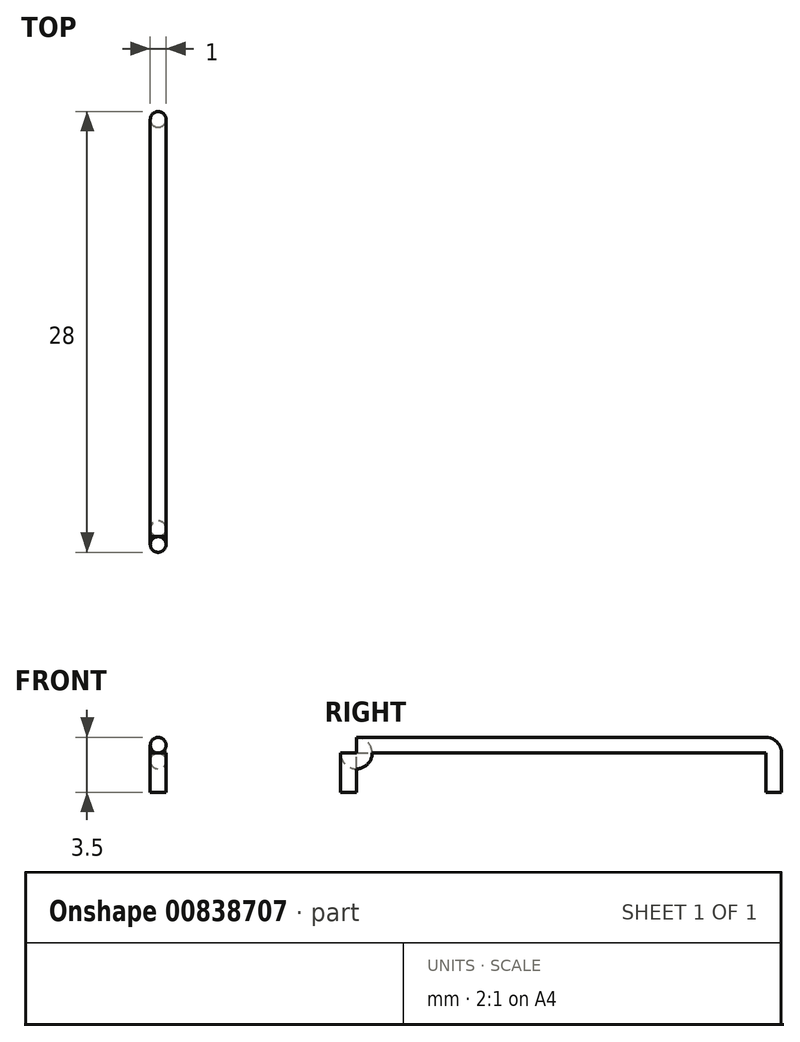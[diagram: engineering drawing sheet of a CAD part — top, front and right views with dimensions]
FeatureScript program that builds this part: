
annotation { "Feature Type Name" : "Feature", "Feature Type Description" : "" }
export const myFeature = defineFeature(function(context is Context, id is Id, definition is map)
    precondition{}
    {
        {
            var Q0;
            Q0=qCreatedBy(makeId("Right.planeOp"),FACE);
            var sketch = newSketch(context, id + "F0", { "sketchPlane" : qUnion([Q0])});
            skLineSegment(sketch, "E0", {"start": v(-13.5, 0) * mm, "end": v(-13.5, 2.5) * mm});
            skLineSegment(sketch, "E1", {"start": v(-13, 3) * mm, "end": v(13, 3) * mm});
            skLineSegment(sketch, "E2", {"start": v(13.5, 2.5) * mm, "end": v(13.5, 0) * mm});
            skPoint(sketch, "E3.visualSharp", {"position": v(-13.5, 3) * mm});
            skArc(sketch, "E3.filletArc", {"start": v(-13, 3) * mm, "mid": v(-13.35, 2.85) * mm, "end": v(-13.5, 2.5) * mm});
            skPoint(sketch, "E4.visualSharp", {"position": v(13.5, 3) * mm});
            skArc(sketch, "E4.filletArc", {"start": v(13.5, 2.5) * mm, "mid": v(13.35, 2.85) * mm, "end": v(13, 3) * mm});
            skSolve(sketch);
        }
        {
            var Q0;
            Q0=qCreatedBy(makeId("Top.planeOp"),FACE);
            var sketch = newSketch(context, id + "F1", { "sketchPlane" : qUnion([Q0])});
            skCircle(sketch, "E5", {"center": v(0, -13.5) * mm, "radius": 0.5 * mm});
            skSolve(sketch);
        }
        {
            var Q0;
            Q0=makeQuery(id+"F1.imprint","IMPRINT",FACE,{"disambiguationData":[TD([[makeQuery(id+"F1.imprint","IMPRINT",EDGE,{"derivedFrom":sQuery(id+"F1.wireOp",EDGE,"E5")}),1.0]])]});
            var Q1;
            Q1=sQuery(id+"F0.wireOp",EDGE,"E0");
            var Q2;
            Q2=sQuery(id+"F0.wireOp",EDGE,"E3.filletArc");
            var Q3;
            Q3=sQuery(id+"F0.wireOp",EDGE,"E1");
            var Q4;
            Q4=sQuery(id+"F0.wireOp",EDGE,"E4.filletArc");
            var Q5;
            Q5=sQuery(id+"F0.wireOp",EDGE,"E2");
            sweep(context, id + "F2", {"profiles" : qUnion([Q0]), "path" : qUnion([Q1, Q2, Q3, Q4, Q5])});
        }
    });
